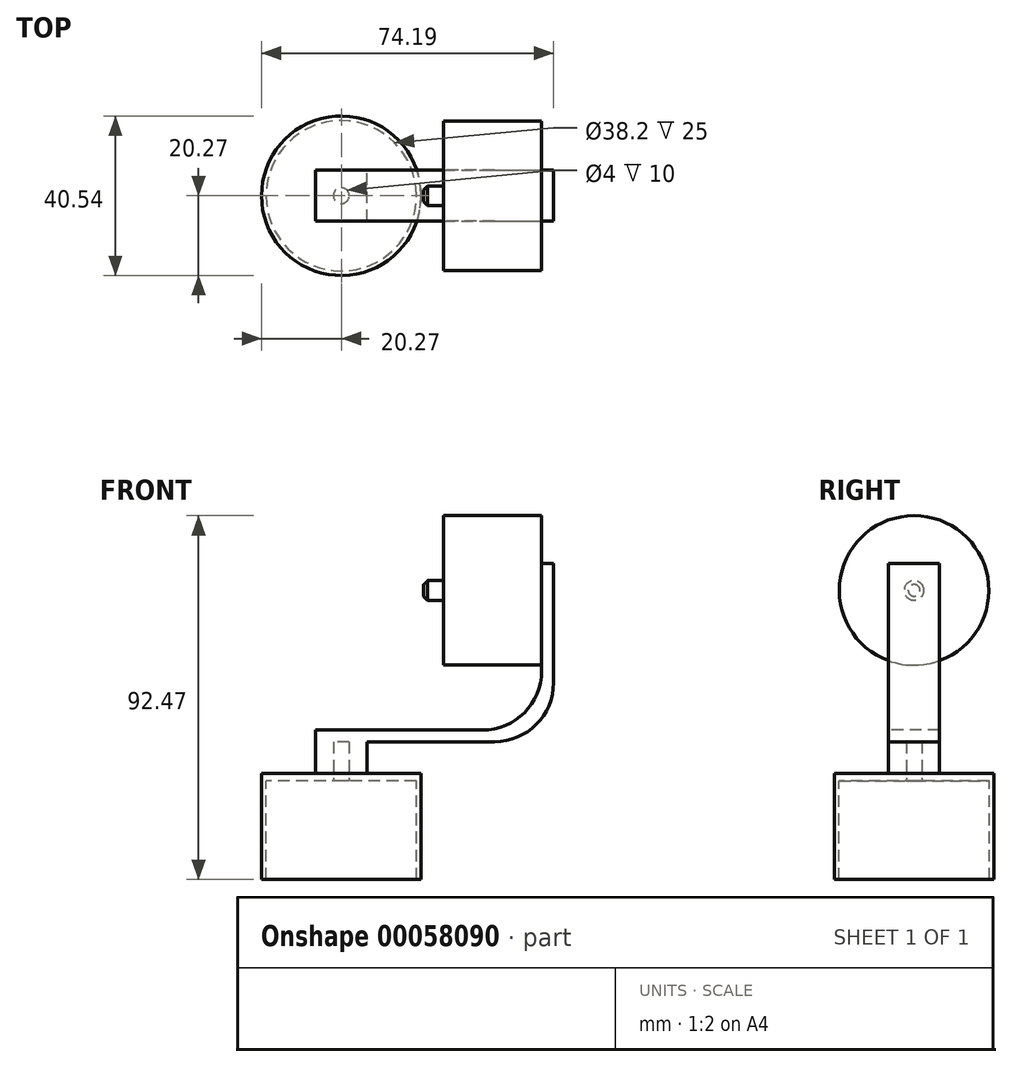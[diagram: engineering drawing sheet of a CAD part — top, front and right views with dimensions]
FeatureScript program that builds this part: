
annotation { "Feature Type Name" : "Feature", "Feature Type Description" : "" }
export const myFeature = defineFeature(function(context is Context, id is Id, definition is map)
    precondition{}
    {
        {
            var Q0;
            Q0=qCreatedBy(makeId("Top.planeOp"),FACE);
            var sketch = newSketch(context, id + "F0", { "sketchPlane" : qUnion([Q0])});
            skCircle(sketch, "E0", {"center": v(0, 0) * mm, "radius": 19.1 * mm});
            skCircle(sketch, "E1", {"center": v(0, 0) * mm, "radius": 20.27 * mm});
            skCircle(sketch, "E2", {"center": v(0, 0) * mm, "radius": 2 * mm});
            skSolve(sketch);
        }
        {
            var Q0;
            Q0=makeQuery(id+"F0.imprint","IMPRINT",FACE,{"disambiguationData":[TD([[makeQuery(id+"F0.imprint","IMPRINT",EDGE,{"derivedFrom":sQuery(id+"F0.wireOp",EDGE,"E0")}),-1.0]])]});
            extrude(context, id + "F1", {"entities" : qUnion([Q0]), "oppositeDirection" : true, "depth" : 25 * mm});
        }
        {
            var Q0;
            Q0=makeQuery(id+"F0.imprint","IMPRINT",FACE,{"disambiguationData":[TD([[makeQuery(id+"F0.imprint","IMPRINT",EDGE,{"derivedFrom":sQuery(id+"F0.wireOp",EDGE,"E0")}),1.0]])]});
            var Q1;
            Q1=makeQuery(id+"F0.imprint","IMPRINT",FACE,{"disambiguationData":[TD([[makeQuery(id+"F0.imprint","IMPRINT",EDGE,{"derivedFrom":sQuery(id+"F0.wireOp",EDGE,"E0")}),-1.0]])]});
            extrude(context, id + "F2", {"entities" : qUnion([Q0, Q1]), "operationType" : NewBodyOperationType.ADD, "depth" : 2 * mm});
        }
        {
            var Q0;
            Q0=makeQuery(id+"F0.imprint","IMPRINT",FACE,{"disambiguationData":[TD([[makeQuery(id+"F0.imprint","IMPRINT",EDGE,{"derivedFrom":sQuery(id+"F0.wireOp",EDGE,"E2")}),1.0]])]});
            var sketch = newSketch(context, id + "F3", { "sketchPlane" : qUnion([Q0])});
            skLineSegment(sketch, "E3.rect.bottom", {"start": v(6.5, 6.5) * mm, "end": v(-6.5, 6.5) * mm});
            skLineSegment(sketch, "E3.rect.top", {"start": v(6.5, -6.5) * mm, "end": v(-6.5, -6.5) * mm});
            skLineSegment(sketch, "E3.rect.left", {"start": v(6.5, 6.5) * mm, "end": v(6.5, -6.5) * mm});
            skLineSegment(sketch, "E3.rect.right", {"start": v(-6.5, 6.5) * mm, "end": v(-6.5, -6.5) * mm});
            skPoint(sketch, "E3.rect.middle", {"position": v(0, 0) * mm});
            skSolve(sketch);
        }
        {
            var Q0;
            Q0=makeQuery(id+"F0.imprint","IMPRINT",FACE,{"disambiguationData":[TD([[makeQuery(id+"F0.imprint","IMPRINT",EDGE,{"derivedFrom":sQuery(id+"F0.wireOp",EDGE,"E2")}),1.0]])]});
            extrude(context, id + "F4", {"entities" : qUnion([Q0]), "operationType" : NewBodyOperationType.REMOVE, "depth" : 5 * mm});
        }
        {
            var Q0;
            Q0=makeQuery(id+"F3.imprint","IMPRINT",FACE,{"disambiguationData":[TD([[makeQuery(id+"F3.imprint","IMPRINT",EDGE,{"derivedFrom":sQuery(id+"F3.wireOp",EDGE,"E3.rect.bottom")}),1.0]])]});
            extrude(context, id + "F5", {"entities" : qUnion([Q0]), "operationType" : NewBodyOperationType.ADD, "depth" : 10 * mm});
        }
        {
            var Q0;
            Q0=makeQuery(id+"F5.opExtrude","SWEPT_FACE",FACE,{"disambiguationData":[OSD([sQuery(id+"F3.wireOp",EDGE,"E3.rect.top")])]});
            var sketch = newSketch(context, id + "F6", { "sketchPlane" : qUnion([Q0])});
            skLineSegment(sketch, "E4.bottom", {"start": v(-6.5, 10) * mm, "end": v(38.92, 10) * mm});
            skLineSegment(sketch, "E4.top", {"start": v(-6.5, 13) * mm, "end": v(35.92, 13) * mm});
            skLineSegment(sketch, "E4.left", {"start": v(-6.5, 10) * mm, "end": v(-6.5, 13) * mm});
            skLineSegment(sketch, "E5.top", {"start": v(53.92, 55.3) * mm, "end": v(50.92, 55.3) * mm});
            skLineSegment(sketch, "E5.left", {"start": v(53.92, 25) * mm, "end": v(53.92, 55.3) * mm});
            skLineSegment(sketch, "E5.right", {"start": v(50.92, 28) * mm, "end": v(50.92, 55.3) * mm});
            skArc(sketch, "E6.filletArc", {"start": v(35.92, 13) * mm, "mid": v(46.53, 17.4) * mm, "end": v(50.92, 28) * mm});
            skLineSegment(sketch, "E7", {"start": v(43.92, 13) * mm, "end": v(43.92, 10) * mm});
            skLineSegment(sketch, "E8", {"start": v(43.92, 10) * mm, "end": v(43.5, 10) * mm});
            skPoint(sketch, "E9.newPointA", {"position": v(43.5, 10) * mm});
            skArc(sketch, "E9.filletArc", {"start": v(38.92, 10) * mm, "mid": v(49.53, 14.4) * mm, "end": v(53.92, 25) * mm});
            skSolve(sketch);
        }
        {
            var Q0;
            Q0=makeQuery(id+"F6.imprint","IMPRINT",FACE,{"disambiguationData":[TD([[makeQuery(id+"F6.imprint","IMPRINT",EDGE,{"derivedFrom":sQuery(id+"F6.wireOp",EDGE,"E4.top")}),-1.0]])]});
            extrude(context, id + "F7", {"entities" : qUnion([Q0]), "operationType" : NewBodyOperationType.ADD, "oppositeDirection" : true, "depth" : 13 * mm});
        }
        {
            var Q0;
            Q0=makeQuery(id+"F7.opExtrude","SWEPT_FACE",FACE,{"disambiguationData":[OSD([sQuery(id+"F6.wireOp",EDGE,"E5.right")])]});
            var sketch = newSketch(context, id + "F8", { "sketchPlane" : qUnion([Q0])});
            skCircle(sketch, "E10", {"center": v(0, 48.47) * mm, "radius": 19 * mm});
            skSolve(sketch);
        }
        {
            var Q0;
            Q0 = qSketchRegion(id + "F8", true);
            var Q1;
            {var subQ1=sQuery(id+"F6.wireOp",EDGE,"E5.right");var subQ6=makeQuery(id+"F7.opExtrude","SWEPT_EDGE",EDGE,{"disambiguationData":[OSD([sQuery(id+"F6.wireOp",EDGE,"E5.top"),subQ1])]});Q1=makeQuery(id+"F8.imprint","IMPRINT",FACE,{"disambiguationData":[TD([[makeQuery(id+"F8.imprint","IMPRINT",EDGE,{"derivedFrom":subQ6}),1.0]])]});}
            extrude(context, id + "F9", {"entities" : qUnion([Q0, Q1]), "operationType" : NewBodyOperationType.ADD, "depth" : 25 * mm});
        }
        {
            var Q0;
            Q0=makeQuery(id+"F9.opExtrude","CAP_FACE",FACE,{"disambiguationData":[OSD([sQuery(id+"F8.wireOp",EDGE,"E10")])],"isStart":false});
            var sketch = newSketch(context, id + "F10", { "sketchPlane" : qUnion([Q0])});
            skCircle(sketch, "E11", {"center": v(0, 48.47) * mm, "radius": 2.5 * mm});
            skSolve(sketch);
        }
        {
            var Q0;
            Q0 = qSketchRegion(id + "F10", true);
            var Q1;
            Q1=makeQuery(id+"F10.imprint","IMPRINT",FACE,{"disambiguationData":[TD([[makeQuery(id+"F10.imprint","IMPRINT",EDGE,{"derivedFrom":sQuery(id+"F10.wireOp",EDGE,"E11")}),1.0]])]});
            extrude(context, id + "F11", {"entities" : qUnion([Q0, Q1]), "operationType" : NewBodyOperationType.ADD, "depth" : 5 * mm});
        }
        {
            var Q0;
            Q0=makeQuery(id+"F11.opExtrude","CAP_EDGE",EDGE,{"disambiguationData":[OSD([sQuery(id+"F10.wireOp",EDGE,"E11")])],"isStart":false});
            chamfer(context, id + "F12", {"entities" : qUnion([Q0]), "width" : 1 * mm, "tangentPropagation" : true});
        }
    });
